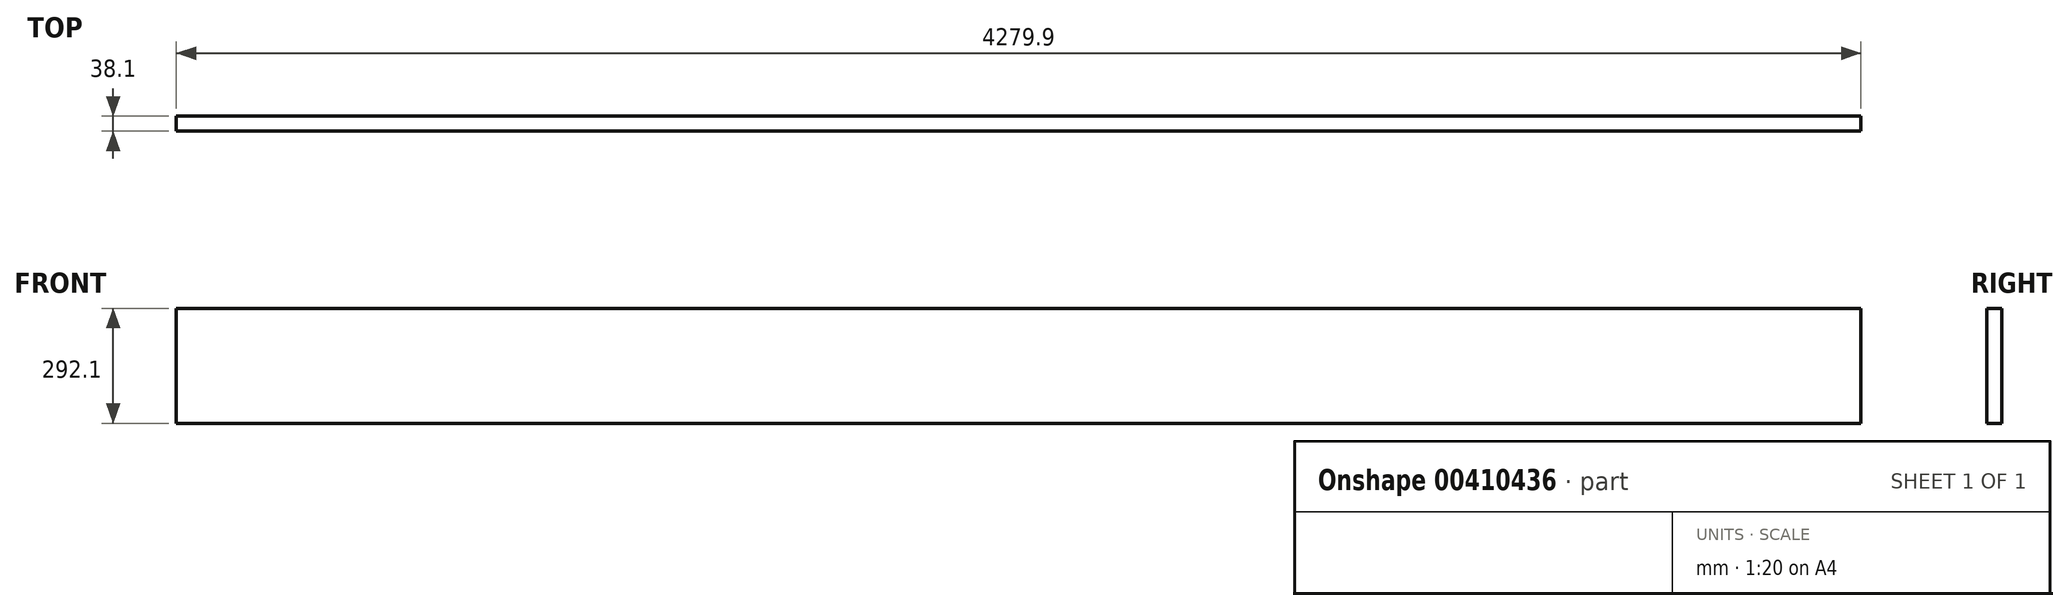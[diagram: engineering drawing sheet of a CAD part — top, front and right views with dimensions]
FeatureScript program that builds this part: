
annotation { "Feature Type Name" : "Feature", "Feature Type Description" : "" }
export const myFeature = defineFeature(function(context is Context, id is Id, definition is map)
    precondition{}
    {
        {
            var Q0;
            Q0=qCreatedBy(makeId("Front.planeOp"),FACE);
            var sketch = newSketch(context, id + "F0", { "sketchPlane" : qUnion([Q0])});
            skLineSegment(sketch, "E0.bottom", {"start": v(-2139.95, 146.05) * mm, "end": v(2139.95, 146.05) * mm});
            skLineSegment(sketch, "E0.top", {"start": v(-2139.95, -146.05) * mm, "end": v(2139.95, -146.05) * mm});
            skLineSegment(sketch, "E0.left", {"start": v(-2139.95, 146.05) * mm, "end": v(-2139.95, -146.05) * mm});
            skLineSegment(sketch, "E0.right", {"start": v(2139.95, 146.05) * mm, "end": v(2139.95, -146.05) * mm});
            skPoint(sketch, "E0.middle", {"position": v(0, 0) * mm});
            skSolve(sketch);
        }
        {
            var Q0;
            Q0 = qSketchRegion(id + "F0", true);
            extrude(context, id + "F1", {"entities" : qUnion([Q0]), "depth" : 38.1 * mm, "offsetDistance" : 25.4 * mm});
        }
    });
